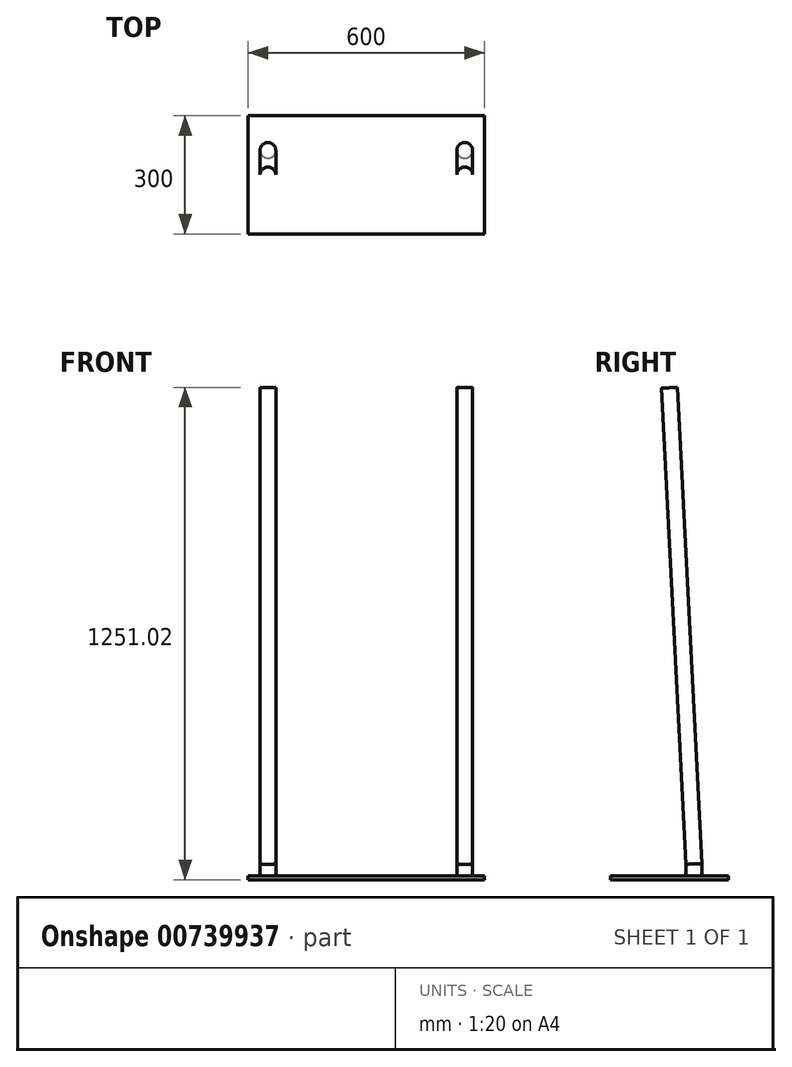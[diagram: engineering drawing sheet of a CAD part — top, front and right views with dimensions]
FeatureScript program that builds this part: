
annotation { "Feature Type Name" : "Feature", "Feature Type Description" : "" }
export const myFeature = defineFeature(function(context is Context, id is Id, definition is map)
    precondition{}
    {
        {
            var Q0;
            Q0=qCreatedBy(makeId("Top.planeOp"),FACE);
            var sketch = newSketch(context, id + "F0", { "sketchPlane" : qUnion([Q0])});
            skLineSegment(sketch, "E0.bottom", {"start": v(300, 150) * mm, "end": v(-300, 150) * mm});
            skLineSegment(sketch, "E0.top", {"start": v(300, -150) * mm, "end": v(-300, -150) * mm});
            skLineSegment(sketch, "E0.left", {"start": v(300, 150) * mm, "end": v(300, -150) * mm});
            skLineSegment(sketch, "E0.right", {"start": v(-300, 150) * mm, "end": v(-300, -150) * mm});
            skPoint(sketch, "E0.middle", {"position": v(0, 0) * mm});
            skSolve(sketch);
        }
        {
            var Q0;
            Q0=makeQuery(id+"F0.imprint","IMPRINT",FACE,{"disambiguationData":[TD([[makeQuery(id+"F0.imprint","IMPRINT",EDGE,{"derivedFrom":sQuery(id+"F0.wireOp",EDGE,"E0.bottom")}),1.0]])]});
            extrude(context, id + "F1", {"entities" : qUnion([Q0]), "depth" : 10 * mm, "offsetDistance" : 25 * mm});
        }
        {
            var Q0;
            Q0=makeQuery(id+"F1.opExtrude","CAP_FACE",FACE,{"disambiguationData":[OSD([sQuery(id+"F0.wireOp",EDGE,"E0.bottom"),sQuery(id+"F0.wireOp",EDGE,"E0.top"),sQuery(id+"F0.wireOp",EDGE,"E0.left"),sQuery(id+"F0.wireOp",EDGE,"E0.right")])],"isStart":false});
            var sketch = newSketch(context, id + "F2", { "sketchPlane" : qUnion([Q0])});
            skCircle(sketch, "E1", {"center": v(-250, 62.06) * mm, "radius": 20 * mm});
            skCircle(sketch, "E2", {"center": v(250, 62.06) * mm, "radius": 20 * mm});
            skLineSegment(sketch, "E3", {"start": v(-250, 62.06) * mm, "end": v(-300, 62.06) * mm});
            skLineSegment(sketch, "E4", {"start": v(250, 62.06) * mm, "end": v(300, 62.06) * mm});
            skSolve(sketch);
        }
        {
            var Q0;
            Q0=makeQuery(id+"F1.opExtrude","SWEPT_FACE",FACE,{"disambiguationData":[OSD([sQuery(id+"F0.wireOp",EDGE,"E0.left")])]});
            cPlane(context, id + "F3", {"entities" : qUnion([Q0]), "cplaneType" : CPlaneType.OFFSET, "offset" : 50 * mm, "oppositeDirection" : true, "width" : 150 * mm, "height" : 150 * mm});
        }
        {
            var Q0;
            Q0=qCreatedBy(id+"F3.planeOp",FACE);
            var sketch = newSketch(context, id + "F4", { "sketchPlane" : qUnion([Q0])});
            skPoint(sketch, "E5.0", {"position": v(62.06, 10) * mm});
            skLineSegment(sketch, "E6", {"start": v(62.06, 10) * mm, "end": v(62.06, 40) * mm});
            skLineSegment(sketch, "E7", {"start": v(62.06, 40) * mm, "end": v(0, 1250) * mm});
            skSolve(sketch);
        }
        {
            var Q0;
            Q0=makeQuery(id+"F2.imprint","IMPRINT",FACE,{"disambiguationData":[TD([[makeQuery(id+"F2.imprint","IMPRINT",EDGE,{"derivedFrom":sQuery(id+"F2.wireOp",EDGE,"E2")}),1.0]])]});
            var Q1;
            Q1=makeQuery(id+"F2.imprint","IMPRINT",FACE,{"disambiguationData":[TD([[makeQuery(id+"F2.imprint","IMPRINT",EDGE,{"derivedFrom":sQuery(id+"F2.wireOp",EDGE,"E1")}),1.0]])]});
            var Q2;
            Q2=sQuery(id+"F4.wireOp",EDGE,"E6");
            var Q3;
            Q3=sQuery(id+"F4.wireOp",EDGE,"E7");
            sweep(context, id + "F5", {"operationType" : NewBodyOperationType.ADD, "profiles" : qUnion([Q0, Q1]), "path" : qUnion([Q2, Q3])});
        }
    });
